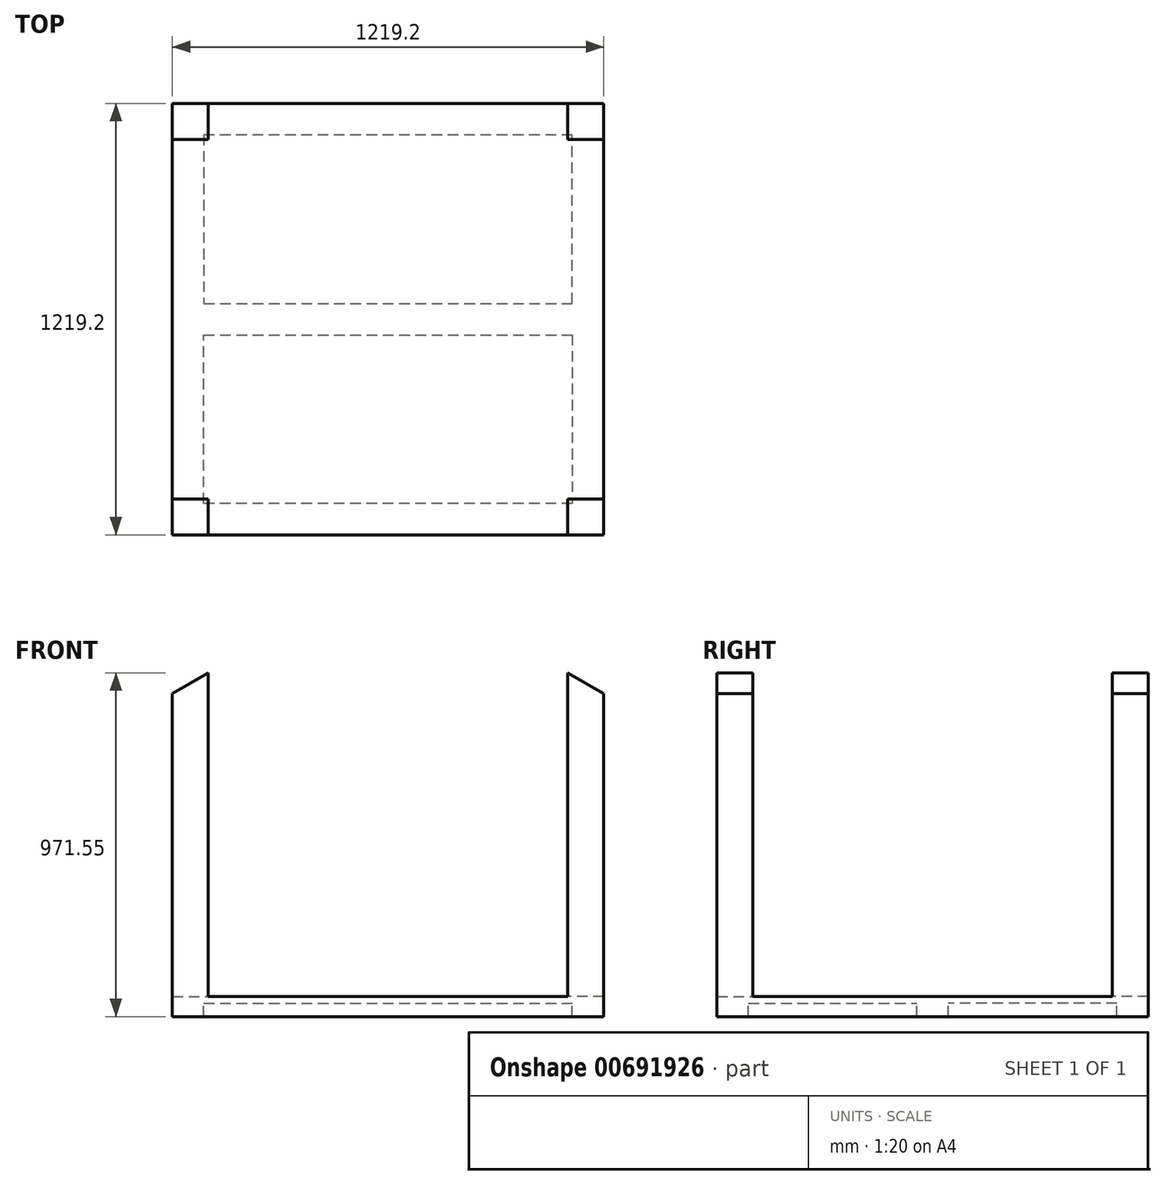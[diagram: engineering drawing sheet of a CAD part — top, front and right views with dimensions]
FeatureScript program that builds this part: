
annotation { "Feature Type Name" : "Feature", "Feature Type Description" : "" }
export const myFeature = defineFeature(function(context is Context, id is Id, definition is map)
    precondition{}
    {
        {
            var Q0;
            Q0=qCreatedBy(makeId("Top.planeOp"),FACE);
            var sketch = newSketch(context, id + "F0", { "sketchPlane" : qUnion([Q0])});
            skLineSegment(sketch, "E0.bottom", {"start": v(0, 0) * mm, "end": v(1219.2, 0) * mm});
            skLineSegment(sketch, "E0.top", {"start": v(0, 1219.2) * mm, "end": v(1219.2, 1219.2) * mm});
            skLineSegment(sketch, "E0.left", {"start": v(0, 0) * mm, "end": v(0, 1219.2) * mm});
            skLineSegment(sketch, "E0.right", {"start": v(1219.2, 0) * mm, "end": v(1219.2, 1219.2) * mm});
            skSolve(sketch);
        }
        {
            var Q0;
            Q0=makeQuery(id+"F0.imprint","IMPRINT",FACE,{"disambiguationData":[TD([[makeQuery(id+"F0.imprint","IMPRINT",EDGE,{"derivedFrom":sQuery(id+"F0.wireOp",EDGE,"E0.bottom")}),1.0]])]});
            extrude(context, id + "F1", {"entities" : qUnion([Q0]), "depth" : 19.05 * mm, "offsetDistance" : 25.4 * mm});
        }
        {
            var Q0;
            Q0=makeQuery(id+"F1.opExtrude","CAP_FACE",FACE,{"disambiguationData":[OSD([sQuery(id+"F0.wireOp",EDGE,"E0.bottom"),sQuery(id+"F0.wireOp",EDGE,"E0.top"),sQuery(id+"F0.wireOp",EDGE,"E0.left"),sQuery(id+"F0.wireOp",EDGE,"E0.right")])],"isStart":true});
            var sketch = newSketch(context, id + "F2", { "sketchPlane" : qUnion([Q0])});
            skLineSegment(sketch, "E1", {"start": v(0, 0) * mm, "end": v(0, -1219.2) * mm});
            skLineSegment(sketch, "E2", {"start": v(0, -1219.2) * mm, "end": v(1219.2, -1219.2) * mm});
            skLineSegment(sketch, "E3", {"start": v(1219.2, -1219.2) * mm, "end": v(1219.2, 0) * mm});
            skLineSegment(sketch, "E4", {"start": v(1219.2, 0) * mm, "end": v(0, 0) * mm});
            skLineSegment(sketch, "E5", {"start": v(88.9, -88.9) * mm, "end": v(88.9, -565.15) * mm});
            skLineSegment(sketch, "E6", {"start": v(88.9, -565.15) * mm, "end": v(1130.3, -565.15) * mm});
            skLineSegment(sketch, "E7", {"start": v(1130.3, -565.15) * mm, "end": v(1130.3, -88.9) * mm});
            skLineSegment(sketch, "E8", {"start": v(1130.3, -88.9) * mm, "end": v(88.9, -88.9) * mm});
            skLineSegment(sketch, "E9", {"start": v(88.9, -654.05) * mm, "end": v(1130.3, -654.05) * mm});
            skLineSegment(sketch, "E10", {"start": v(1130.3, -654.05) * mm, "end": v(1130.3, -1130.3) * mm});
            skLineSegment(sketch, "E11", {"start": v(1130.3, -1130.3) * mm, "end": v(88.9, -1130.3) * mm});
            skLineSegment(sketch, "E12", {"start": v(88.9, -1130.3) * mm, "end": v(88.9, -654.05) * mm});
            skLineSegment(sketch, "E13", {"start": v(1130.3, -654.05) * mm, "end": v(1130.3, -565.15) * mm, "construction": true});
            skSolve(sketch);
        }
        {
            var Q0;
            Q0 = qSketchRegion(id + "F2", true);
            extrude(context, id + "F3", {"entities" : qUnion([Q0]), "operationType" : NewBodyOperationType.ADD, "depth" : 38.1 * mm, "offsetDistance" : 25.4 * mm});
        }
        {
            var Q0;
            Q0=makeQuery(id+"F1.opExtrude","CAP_FACE",FACE,{"disambiguationData":[OSD([sQuery(id+"F0.wireOp",EDGE,"E0.bottom"),sQuery(id+"F0.wireOp",EDGE,"E0.top"),sQuery(id+"F0.wireOp",EDGE,"E0.left"),sQuery(id+"F0.wireOp",EDGE,"E0.right")])],"isStart":false});
            var sketch = newSketch(context, id + "F4", { "sketchPlane" : qUnion([Q0])});
            skLineSegment(sketch, "E14.bottom", {"start": v(0, 1219.2) * mm, "end": v(101.6, 1219.2) * mm});
            skLineSegment(sketch, "E14.top", {"start": v(0, 1117.6) * mm, "end": v(101.6, 1117.6) * mm});
            skLineSegment(sketch, "E14.left", {"start": v(0, 1219.2) * mm, "end": v(0, 1117.6) * mm});
            skLineSegment(sketch, "E14.right", {"start": v(101.6, 1219.2) * mm, "end": v(101.6, 1117.6) * mm});
            skLineSegment(sketch, "E15.bottom", {"start": v(0, 0) * mm, "end": v(101.6, 0) * mm});
            skLineSegment(sketch, "E15.top", {"start": v(0, 101.6) * mm, "end": v(101.6, 101.6) * mm});
            skLineSegment(sketch, "E15.left", {"start": v(0, 0) * mm, "end": v(0, 101.6) * mm});
            skLineSegment(sketch, "E15.right", {"start": v(101.6, 0) * mm, "end": v(101.6, 101.6) * mm});
            skLineSegment(sketch, "E16.bottom", {"start": v(1219.2, 0) * mm, "end": v(1117.6, 0) * mm});
            skLineSegment(sketch, "E16.top", {"start": v(1219.2, 101.6) * mm, "end": v(1117.6, 101.6) * mm});
            skLineSegment(sketch, "E16.left", {"start": v(1219.2, 0) * mm, "end": v(1219.2, 101.6) * mm});
            skLineSegment(sketch, "E16.right", {"start": v(1117.6, 0) * mm, "end": v(1117.6, 101.6) * mm});
            skLineSegment(sketch, "E17.bottom", {"start": v(1219.2, 1219.2) * mm, "end": v(1117.6, 1219.2) * mm});
            skLineSegment(sketch, "E17.top", {"start": v(1219.2, 1117.6) * mm, "end": v(1117.6, 1117.6) * mm});
            skLineSegment(sketch, "E17.left", {"start": v(1219.2, 1219.2) * mm, "end": v(1219.2, 1117.6) * mm});
            skLineSegment(sketch, "E17.right", {"start": v(1117.6, 1219.2) * mm, "end": v(1117.6, 1117.6) * mm});
            skSolve(sketch);
        }
        {
            var Q0;
            Q0 = qSketchRegion(id + "F4", true);
            extrude(context, id + "F5", {"entities" : qUnion([Q0]), "operationType" : NewBodyOperationType.ADD, "depth" : 914.4 * mm, "offsetDistance" : 25.4 * mm});
        }
        {
            var Q0;
            Q0=makeQuery(id+"F5.boolean.opBoolean","MERGE",FACE,{"derivedFrom":[makeQuery(id+"F3.boolean.opBoolean","MERGE",FACE,{"derivedFrom":[makeQuery(id+"F1.opExtrude","SWEPT_FACE",FACE,{"disambiguationData":[OSD([sQuery(id+"F0.wireOp",EDGE,"E0.bottom")])]}),makeQuery(id+"F3.opExtrude","SWEPT_FACE",FACE,{"disambiguationData":[OSD([sQuery(id+"F2.wireOp",EDGE,"E4")])]})]}),makeQuery(id+"F5.opExtrude","SWEPT_FACE",FACE,{"disambiguationData":[OSD([sQuery(id+"F4.wireOp",EDGE,"E15.bottom")])]}),makeQuery(id+"F5.opExtrude","SWEPT_FACE",FACE,{"disambiguationData":[OSD([sQuery(id+"F4.wireOp",EDGE,"E16.bottom")])]})]});
            var sketch = newSketch(context, id + "F6", { "sketchPlane" : qUnion([Q0])});
            skLineSegment(sketch, "E18", {"start": v(101.6, 933.45) * mm, "end": v(0, 874.8) * mm});
            skLineSegment(sketch, "E19", {"start": v(0, 874.8) * mm, "end": v(0, 933.45) * mm});
            skLineSegment(sketch, "E20", {"start": v(0, 933.45) * mm, "end": v(101.6, 933.45) * mm});
            skLineSegment(sketch, "E21", {"start": v(1117.6, 933.45) * mm, "end": v(1219.2, 933.45) * mm});
            skLineSegment(sketch, "E22", {"start": v(1219.2, 933.45) * mm, "end": v(1219.2, 874.8) * mm});
            skLineSegment(sketch, "E23", {"start": v(1219.2, 874.8) * mm, "end": v(1117.6, 933.45) * mm});
            skSolve(sketch);
        }
        {
            var Q0;
            Q0=makeQuery(id+"F6.imprint","IMPRINT",FACE,{"disambiguationData":[TD([[makeQuery(id+"F6.imprint","IMPRINT",EDGE,{"derivedFrom":sQuery(id+"F6.wireOp",EDGE,"E18")}),-1.0]])]});
            var Q1;
            Q1=makeQuery(id+"F6.imprint","IMPRINT",FACE,{"disambiguationData":[TD([[makeQuery(id+"F6.imprint","IMPRINT",EDGE,{"derivedFrom":sQuery(id+"F6.wireOp",EDGE,"E21")}),-1.0]])]});
            extrude(context, id + "F7", {"entities" : qUnion([Q0, Q1]), "operationType" : NewBodyOperationType.REMOVE, "endBound" : BoundingType.THROUGH_ALL, "depth" : 25.4 * mm, "offsetDistance" : 25.4 * mm, "hasSecondDirection" : true, "secondDirectionBound" : SecondDirectionBoundingType.THROUGH_ALL, "secondDirectionOppositeDirection" : true, "secondDirectionDepth" : 25.4 * mm});
        }
    });
